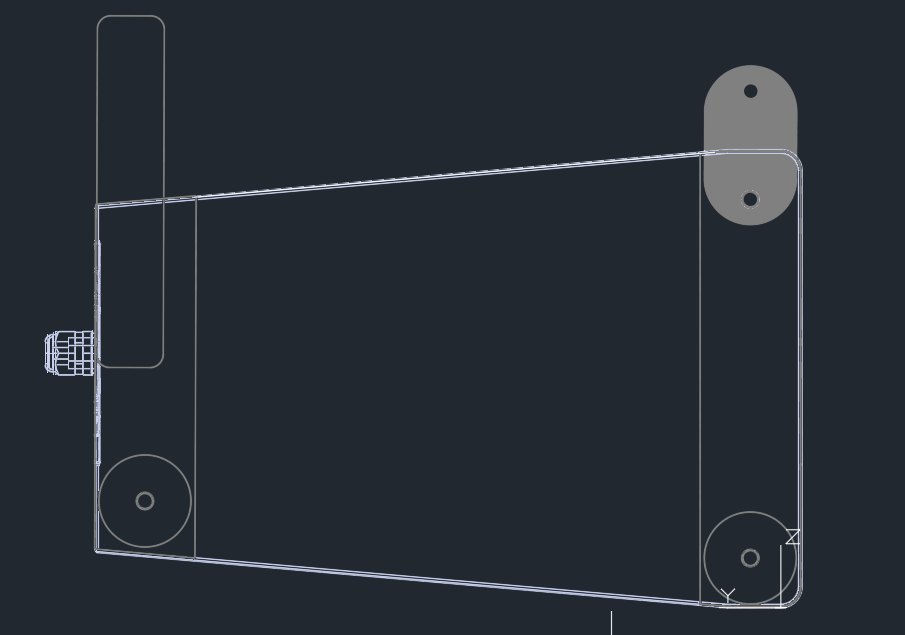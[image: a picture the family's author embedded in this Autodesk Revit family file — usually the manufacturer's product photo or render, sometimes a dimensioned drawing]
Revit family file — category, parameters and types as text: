
# Revit family: Communication_Bosch_Speakers_X-Line Advance Install X2i
name_source: partatom
category: Communication Devices
revit_build: Autodesk Revit 2018 (Build: 20180423_1000(x64)
units: mm (PartAtom-declared; Revit-internal decimal feet)

## family parameters
Always vertical = No
Cut with Voids When Loaded = No
Maintain Annotation Orientation = No
Part Type = Normal
Room Calculation Point = No
Round Connector Dimension = Use Diameter
Shared = Yes
Work Plane-Based = Yes

## types (8) — shared parameters
ArchitectsAndEngineersSpecs = https://products.electrovoice.com
Default Elevation = 1219 mm
Dimensions (H x W x D) = 347 mm x 678.5 mm x 536 mm
Disclaimer = https://resources-boschsecurity-cdn.azureedge.net
Frequency Response (-3 dB) = Full-space anechoic array performance with FIR-Drive preset (52 Hz - 19 kHz)
Horizontal Coverage = 90° or 120°
IP Rating = IP55 (fiberglass models only)
InstallationManual = https://products.electrovoice.com
Manufacturer = Electro Voice
Material = Multi-ply birch
Max SPL = 145 dB Peak
PlanningTools = https://products.electrovoice.com
Power Handling = 150 W Continuous, 600 Peak
Product Information = https://products.electrovoice.com
Product Website = https://products.electrovoice.com
URL = www.electrovoice.com
UniclassCode = Pr_70_75_36_50
UniclassTitle = Loudspeakers
Vertical Coverage = Array dependent
Weight (Kg) = 34.8
ifcExportAs = IfcElectricApplianceType

## per-type parameters (varying)
| type | Colour | XMTI |
| X2I-212/90-B X2i 12" 90° Install array black | RAL 9005 black | 5 |
| X2I-212/90-W X2i 12" 90° Install array white | RAL 9003 white | 8 |
| X2I-212/90-FGB X2i 12" 90° Install array black FG | RAL 9005 black | 6 |
| X2I-212/90-FGW X2i 12" 90° Install array white FG | RAL 9003 white | 7 |
| X2I-212/120-B X2i 12" 120° Install array black | RAL 9005 black | 1 |
| X2I-212/120-W X2i 12" 120° Install array white | RAL 9003 white | 4 |
| X2I-212/120-FGB X2i 12" 120° Install array black FG | RAL 9005 black | 2 |
| X2I-212/120-FGW X2i 12" 120° Install array white FG | RAL 9003 white | 3 |

## geometry (parser evidence)
native form markers: Sweep x20
no freeform markers — native parametric forms only
